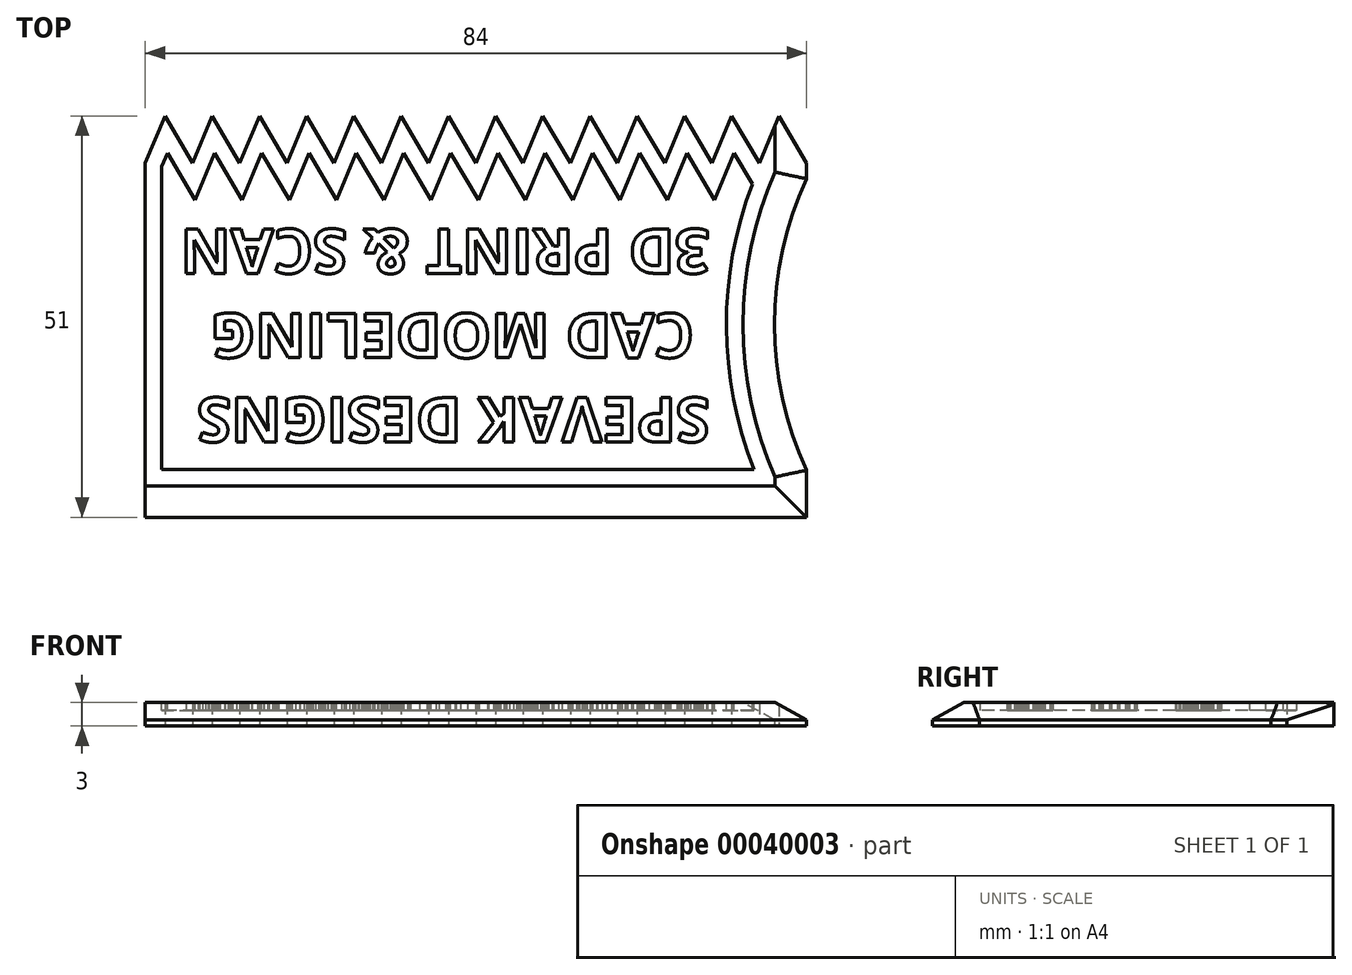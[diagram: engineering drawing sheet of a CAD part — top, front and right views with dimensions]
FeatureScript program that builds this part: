
annotation { "Feature Type Name" : "Feature", "Feature Type Description" : "" }
export const myFeature = defineFeature(function(context is Context, id is Id, definition is map)
    precondition{}
    {
        {
            var Q0;
            Q0=qCreatedBy(makeId("Top.planeOp"),FACE);
            var sketch = newSketch(context, id + "F0", { "sketchPlane" : qUnion([Q0])});
            skLineSegment(sketch, "E0.bottom", {"start": v(0, 0) * mm, "end": v(84, 0) * mm});
            skLineSegment(sketch, "E0.top", {"start": v(2.5, 51) * mm, "end": v(80.5, 51) * mm, "construction": true});
            skLineSegment(sketch, "E0.left", {"start": v(0, 0) * mm, "end": v(0, 45) * mm});
            skLineSegment(sketch, "E0.right", {"start": v(84, 0) * mm, "end": v(84, 45) * mm, "construction": true});
            skLineSegment(sketch, "E1", {"start": v(0, 45) * mm, "end": v(84, 45) * mm, "construction": true});
            skLineSegment(sketch, "E2", {"start": v(0, 45) * mm, "end": v(2.5, 51) * mm});
            skLineSegment(sketch, "E3", {"start": v(2.5, 51) * mm, "end": v(6, 45) * mm});
            skLineSegment(sketch, "E4.1.0.0", {"start": v(6, 45) * mm, "end": v(8.5, 51) * mm});
            skLineSegment(sketch, "E4.1.0.1", {"start": v(8.5, 51) * mm, "end": v(12, 45) * mm});
            skLineSegment(sketch, "E4.2.0.0", {"start": v(12, 45) * mm, "end": v(14.5, 51) * mm});
            skLineSegment(sketch, "E4.2.0.1", {"start": v(14.5, 51) * mm, "end": v(18, 45) * mm});
            skLineSegment(sketch, "E4.3.0.0", {"start": v(18, 45) * mm, "end": v(20.5, 51) * mm});
            skLineSegment(sketch, "E4.3.0.1", {"start": v(20.5, 51) * mm, "end": v(24, 45) * mm});
            skLineSegment(sketch, "E4.4.0.0", {"start": v(24, 45) * mm, "end": v(26.5, 51) * mm});
            skLineSegment(sketch, "E4.4.0.1", {"start": v(26.5, 51) * mm, "end": v(30, 45) * mm});
            skLineSegment(sketch, "E4.5.0.0", {"start": v(30, 45) * mm, "end": v(32.5, 51) * mm});
            skLineSegment(sketch, "E4.5.0.1", {"start": v(32.5, 51) * mm, "end": v(36, 45) * mm});
            skLineSegment(sketch, "E4.6.0.0", {"start": v(36, 45) * mm, "end": v(38.5, 51) * mm});
            skLineSegment(sketch, "E4.6.0.1", {"start": v(38.5, 51) * mm, "end": v(42, 45) * mm});
            skLineSegment(sketch, "E4.7.0.0", {"start": v(42, 45) * mm, "end": v(44.5, 51) * mm});
            skLineSegment(sketch, "E4.7.0.1", {"start": v(44.5, 51) * mm, "end": v(48, 45) * mm});
            skLineSegment(sketch, "E4.8.0.0", {"start": v(48, 45) * mm, "end": v(50.5, 51) * mm});
            skLineSegment(sketch, "E4.8.0.1", {"start": v(50.5, 51) * mm, "end": v(54, 45) * mm});
            skLineSegment(sketch, "E4.9.0.0", {"start": v(54, 45) * mm, "end": v(56.5, 51) * mm});
            skLineSegment(sketch, "E4.9.0.1", {"start": v(56.5, 51) * mm, "end": v(60, 45) * mm});
            skLineSegment(sketch, "E4.10.0.0", {"start": v(60, 45) * mm, "end": v(62.5, 51) * mm});
            skLineSegment(sketch, "E4.10.0.1", {"start": v(62.5, 51) * mm, "end": v(66, 45) * mm});
            skLineSegment(sketch, "E4.11.0.0", {"start": v(66, 45) * mm, "end": v(68.5, 51) * mm});
            skLineSegment(sketch, "E4.11.0.1", {"start": v(68.5, 51) * mm, "end": v(72, 45) * mm});
            skLineSegment(sketch, "E4.12.0.0", {"start": v(72, 45) * mm, "end": v(74.5, 51) * mm});
            skLineSegment(sketch, "E4.12.0.1", {"start": v(74.5, 51) * mm, "end": v(78, 45) * mm});
            skLineSegment(sketch, "E4.13.0.0", {"start": v(78, 45) * mm, "end": v(80.5, 51) * mm});
            skLineSegment(sketch, "E4.13.0.1", {"start": v(80.5, 51) * mm, "end": v(84, 45) * mm});
            skLineSegment(sketch, "E4.direction1", {"start": v(0, 45) * mm, "end": v(6, 45) * mm, "construction": true});
            skLineSegment(sketch, "E5", {"start": v(84, 45) * mm, "end": v(84, 43) * mm});
            skArc(sketch, "E6", {"start": v(84, 43) * mm, "mid": v(79.93, 24.5) * mm, "end": v(84, 6) * mm});
            skLineSegment(sketch, "E7", {"start": v(84, 6) * mm, "end": v(84, 0) * mm});
            skSolve(sketch);
        }
        {
            var Q0;
            Q0=qSketchRegion(id+"F0",true);
            extrude(context, id + "F1", {"entities" : qUnion([Q0]), "depth" : 3 * mm});
        }
        {
            var Q0;
            Q0=makeQuery(id+"F1.opExtrude","CAP_EDGE",EDGE,{"disambiguationData":[OSD([sQuery(id+"F0.wireOp",EDGE,"E5")])],"isStart":false});
            var Q1;
            Q1=makeQuery(id+"F1.opExtrude","CAP_EDGE",EDGE,{"disambiguationData":[OSD([sQuery(id+"F0.wireOp",EDGE,"E6")])],"isStart":false});
            var Q2;
            Q2=makeQuery(id+"F1.opExtrude","CAP_EDGE",EDGE,{"disambiguationData":[OSD([sQuery(id+"F0.wireOp",EDGE,"E0.bottom")])],"isStart":false});
            var Q3;
            Q3=makeQuery(id+"F1.opExtrude","CAP_EDGE",EDGE,{"disambiguationData":[OSD([sQuery(id+"F0.wireOp",EDGE,"E7")])],"isStart":false});
            chamfer(context, id + "F2", {"entities" : qUnion([Q0, Q1, Q2, Q3]), "chamferType" : ChamferType.TWO_OFFSETS, "width1" : 2.2 * mm, "oppositeDirection" : false, "width2" : 4 * mm, "tangentPropagation" : true});
        }
        {
            var Q0;
            Q0=makeQuery(id+"F1.opExtrude","CAP_FACE",FACE,{"disambiguationData":[OSD([sQuery(id+"F0.wireOp",EDGE,"E0.bottom"),sQuery(id+"F0.wireOp",EDGE,"E0.left"),sQuery(id+"F0.wireOp",EDGE,"E2"),sQuery(id+"F0.wireOp",EDGE,"E3"),sQuery(id+"F0.wireOp",EDGE,"E4.1.0.0"),sQuery(id+"F0.wireOp",EDGE,"E4.1.0.1"),sQuery(id+"F0.wireOp",EDGE,"E4.2.0.0"),sQuery(id+"F0.wireOp",EDGE,"E4.2.0.1"),sQuery(id+"F0.wireOp",EDGE,"E4.3.0.0"),sQuery(id+"F0.wireOp",EDGE,"E4.3.0.1"),sQuery(id+"F0.wireOp",EDGE,"E4.4.0.0"),sQuery(id+"F0.wireOp",EDGE,"E4.4.0.1"),sQuery(id+"F0.wireOp",EDGE,"E4.5.0.0"),sQuery(id+"F0.wireOp",EDGE,"E4.5.0.1"),sQuery(id+"F0.wireOp",EDGE,"E4.6.0.0"),sQuery(id+"F0.wireOp",EDGE,"E4.6.0.1"),sQuery(id+"F0.wireOp",EDGE,"E4.7.0.0"),sQuery(id+"F0.wireOp",EDGE,"E4.7.0.1"),sQuery(id+"F0.wireOp",EDGE,"E4.8.0.0"),sQuery(id+"F0.wireOp",EDGE,"E4.8.0.1"),sQuery(id+"F0.wireOp",EDGE,"E4.9.0.0"),sQuery(id+"F0.wireOp",EDGE,"E4.9.0.1"),sQuery(id+"F0.wireOp",EDGE,"E4.10.0.0"),sQuery(id+"F0.wireOp",EDGE,"E4.10.0.1"),sQuery(id+"F0.wireOp",EDGE,"E4.11.0.0"),sQuery(id+"F0.wireOp",EDGE,"E4.11.0.1"),sQuery(id+"F0.wireOp",EDGE,"E4.12.0.0"),sQuery(id+"F0.wireOp",EDGE,"E4.12.0.1"),sQuery(id+"F0.wireOp",EDGE,"E4.13.0.0"),sQuery(id+"F0.wireOp",EDGE,"E4.13.0.1"),sQuery(id+"F0.wireOp",EDGE,"E5"),sQuery(id+"F0.wireOp",EDGE,"E6"),sQuery(id+"F0.wireOp",EDGE,"E7")])],"isStart":false});
            var sketch = newSketch(context, id + "F3", { "sketchPlane" : qUnion([Q0])});
            skLineSegment(sketch, "E8.0", {"start": v(2.1, 44.58) * mm, "end": v(2.1, 6.1) * mm});
            skLineSegment(sketch, "E8.1", {"start": v(2.81, 46.3) * mm, "end": v(2.1, 44.58) * mm});
            skLineSegment(sketch, "E8.2", {"start": v(6.31, 40.3) * mm, "end": v(2.81, 46.3) * mm});
            skLineSegment(sketch, "E8.3", {"start": v(8.81, 46.3) * mm, "end": v(6.31, 40.3) * mm});
            skLineSegment(sketch, "E8.4", {"start": v(12.31, 40.3) * mm, "end": v(8.81, 46.3) * mm});
            skLineSegment(sketch, "E8.5", {"start": v(14.81, 46.3) * mm, "end": v(12.31, 40.3) * mm});
            skLineSegment(sketch, "E8.6", {"start": v(18.31, 40.3) * mm, "end": v(14.81, 46.3) * mm});
            skLineSegment(sketch, "E8.7", {"start": v(2.1, 6.1) * mm, "end": v(77.32, 6.1) * mm});
            skArc(sketch, "E8.8", {"start": v(77.32, 6.1) * mm, "mid": v(73.83, 24.2) * mm, "end": v(77.11, 42.35) * mm});
            skLineSegment(sketch, "E8.9", {"start": v(77.11, 42.35) * mm, "end": v(74.81, 46.3) * mm});
            skLineSegment(sketch, "E8.10", {"start": v(74.81, 46.3) * mm, "end": v(72.31, 40.3) * mm});
            skLineSegment(sketch, "E8.11", {"start": v(72.31, 40.3) * mm, "end": v(68.81, 46.3) * mm});
            skLineSegment(sketch, "E8.12", {"start": v(68.81, 46.3) * mm, "end": v(66.31, 40.3) * mm});
            skLineSegment(sketch, "E8.13", {"start": v(66.31, 40.3) * mm, "end": v(62.81, 46.3) * mm});
            skLineSegment(sketch, "E8.14", {"start": v(62.81, 46.3) * mm, "end": v(60.31, 40.3) * mm});
            skLineSegment(sketch, "E8.15", {"start": v(60.31, 40.3) * mm, "end": v(56.81, 46.3) * mm});
            skLineSegment(sketch, "E8.16", {"start": v(56.81, 46.3) * mm, "end": v(54.31, 40.3) * mm});
            skLineSegment(sketch, "E8.17", {"start": v(54.31, 40.3) * mm, "end": v(50.81, 46.3) * mm});
            skLineSegment(sketch, "E8.18", {"start": v(50.81, 46.3) * mm, "end": v(48.31, 40.3) * mm});
            skLineSegment(sketch, "E8.19", {"start": v(48.31, 40.3) * mm, "end": v(44.81, 46.3) * mm});
            skLineSegment(sketch, "E8.20", {"start": v(44.81, 46.3) * mm, "end": v(42.31, 40.3) * mm});
            skLineSegment(sketch, "E8.21", {"start": v(42.31, 40.3) * mm, "end": v(38.81, 46.3) * mm});
            skLineSegment(sketch, "E8.22", {"start": v(38.81, 46.3) * mm, "end": v(36.31, 40.3) * mm});
            skLineSegment(sketch, "E8.23", {"start": v(36.31, 40.3) * mm, "end": v(32.81, 46.3) * mm});
            skLineSegment(sketch, "E8.24", {"start": v(32.81, 46.3) * mm, "end": v(30.31, 40.3) * mm});
            skLineSegment(sketch, "E8.25", {"start": v(30.31, 40.3) * mm, "end": v(26.81, 46.3) * mm});
            skLineSegment(sketch, "E8.26", {"start": v(26.81, 46.3) * mm, "end": v(24.31, 40.3) * mm});
            skLineSegment(sketch, "E8.27", {"start": v(24.31, 40.3) * mm, "end": v(20.81, 46.3) * mm});
            skLineSegment(sketch, "E8.28", {"start": v(20.81, 46.3) * mm, "end": v(18.31, 40.3) * mm});
            skSolve(sketch);
        }
        {
            var Q0;
            Q0=makeQuery(id+"F3.imprint","IMPRINT",FACE,{"disambiguationData":[TD([[makeQuery(id+"F3.imprint","IMPRINT",EDGE,{"derivedFrom":sQuery(id+"F3.wireOp",EDGE,"E8.0")}),1.0]])]});
            extrude(context, id + "F4", {"entities" : qUnion([Q0]), "operationType" : NewBodyOperationType.REMOVE, "oppositeDirection" : true, "depth" : 1 * mm});
        }
        {
            var Q0;
            Q0=makeQuery(id+"F4.boolean.opBoolean","COPY",FACE,{"derivedFrom":makeQuery(id+"F4.opExtrude","CAP_FACE",FACE,{"disambiguationData":[OSD([sQuery(id+"F3.wireOp",EDGE,"E8.0"),sQuery(id+"F3.wireOp",EDGE,"E8.1"),sQuery(id+"F3.wireOp",EDGE,"E8.2"),sQuery(id+"F3.wireOp",EDGE,"E8.3"),sQuery(id+"F3.wireOp",EDGE,"E8.4"),sQuery(id+"F3.wireOp",EDGE,"E8.5"),sQuery(id+"F3.wireOp",EDGE,"E8.6"),sQuery(id+"F3.wireOp",EDGE,"E8.7"),sQuery(id+"F3.wireOp",EDGE,"E8.8"),sQuery(id+"F3.wireOp",EDGE,"E8.9"),sQuery(id+"F3.wireOp",EDGE,"E8.10"),sQuery(id+"F3.wireOp",EDGE,"E8.11"),sQuery(id+"F3.wireOp",EDGE,"E8.12"),sQuery(id+"F3.wireOp",EDGE,"E8.13"),sQuery(id+"F3.wireOp",EDGE,"E8.14"),sQuery(id+"F3.wireOp",EDGE,"E8.15"),sQuery(id+"F3.wireOp",EDGE,"E8.16"),sQuery(id+"F3.wireOp",EDGE,"E8.17"),sQuery(id+"F3.wireOp",EDGE,"E8.18"),sQuery(id+"F3.wireOp",EDGE,"E8.19"),sQuery(id+"F3.wireOp",EDGE,"E8.20"),sQuery(id+"F3.wireOp",EDGE,"E8.21"),sQuery(id+"F3.wireOp",EDGE,"E8.22"),sQuery(id+"F3.wireOp",EDGE,"E8.23"),sQuery(id+"F3.wireOp",EDGE,"E8.24"),sQuery(id+"F3.wireOp",EDGE,"E8.25"),sQuery(id+"F3.wireOp",EDGE,"E8.26"),sQuery(id+"F3.wireOp",EDGE,"E8.27"),sQuery(id+"F3.wireOp",EDGE,"E8.28")])],"isStart":false})});
            var sketch = newSketch(context, id + "F5", { "sketchPlane" : qUnion([Q0])});
            skLineSegment(sketch, "E9", {"start": v(39.71, 6.1) * mm, "end": v(39.71, 40.3) * mm, "construction": true});
            skText(sketch, "E10", { "text": "SPEVAK DESIGNS\n CAD MODELING\n3D PRINT & SCAN", "fontName": "OpenSans-Bold.ttf"});
            const initialGuessF5  = {"E10": [0.07174, 0.0152, -1, 0, 0.00567]};
            skSetInitialGuess(sketch, initialGuessF5);
            skSolve(sketch);
        }
        {
            var Q0;
            Q0=qSketchRegion(id+"F5",true);
            extrude(context, id + "F6", {"entities" : qUnion([Q0]), "operationType" : NewBodyOperationType.ADD, "depth" : 1 * mm});
        }
    });
